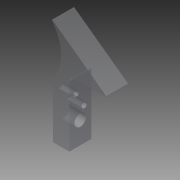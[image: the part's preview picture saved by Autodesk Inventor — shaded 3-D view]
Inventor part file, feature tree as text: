
AUTODESK INVENTOR PART (.ipt)
format: ipt  version: 2013 (Build 170138000, 138)  size: 112,128 bytes
history: native  units: in
note: dims shown in document units (in); Inventor stores cm internally (conversion verified against a paired STEP export)
features: fillet x4, extrude x2, sketch x2
ambient origin geometry x8: Origin, YZ Plane, XZ Plane, XY Plane, X Axis, Y Axis, Z Axis, Center Point
bodies: Solid1 (feature_tree)
feature tree (8):
  extrude  "Extrusion1"  Depth=1.5in
  extrude  "Extrusion2"  Depth=2.5in
  fillet  "Fillet1"  Radius=0.125in
  fillet  "Fillet2"  Radius=0.1875in
  fillet  "Fillet3"  Radius=0.5in
  fillet  "Fillet4"  Radius=0.266in
  sketch  "Sketch1"  dims[d0=0.375in d1=1.5in]
  sketch  "Sketch2"  dims[d2=0.875in d3=2.5in d4=0.125in d5=0.1875in d6=0.5in d7=0.0in d8=0.266in d10=0.25in d11=0.5in d12=0.125in d13=0.125in d14=0.3125in d15=0.1875in d16=0.1562in d17=0.75in d18=0.5in d19=0.0in d20=0.125in d21=0.0125in d22=0.0125in d23=0.0125in]
